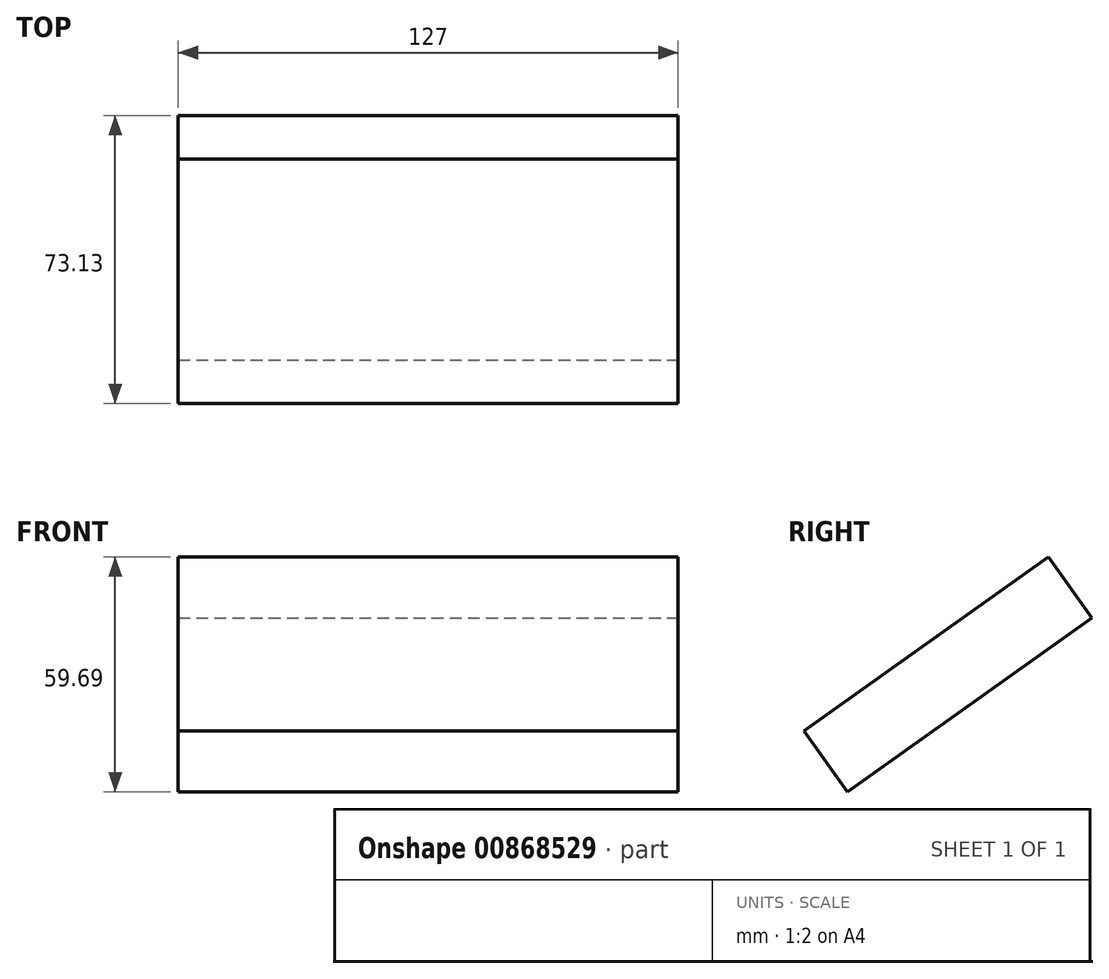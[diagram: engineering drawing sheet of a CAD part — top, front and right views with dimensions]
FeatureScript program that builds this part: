
annotation { "Feature Type Name" : "Feature", "Feature Type Description" : "" }
export const myFeature = defineFeature(function(context is Context, id is Id, definition is map)
    precondition{}
    {
        {
            var Q0;
            Q0=qCreatedBy(makeId("Right.planeOp"),FACE);
            var sketch = newSketch(context, id + "F0", { "sketchPlane" : qUnion([Q0])});
            skLineSegment(sketch, "E0", {"start": v(0, 0) * mm, "end": v(-11.04, 15.52) * mm});
            skLineSegment(sketch, "E1", {"start": v(-11.04, 15.52) * mm, "end": v(51.05, 59.7) * mm});
            skLineSegment(sketch, "E2", {"start": v(51.05, 59.7) * mm, "end": v(62.1, 44.17) * mm});
            skLineSegment(sketch, "E3", {"start": v(0, 0) * mm, "end": v(62.1, 44.17) * mm});
            skSolve(sketch);
        }
        {
            var Q0;
            Q0=makeQuery(id+"F0.imprint","IMPRINT",FACE,{"disambiguationData":[TD([[makeQuery(id+"F0.imprint","IMPRINT",EDGE,{"derivedFrom":sQuery(id+"F0.wireOp",EDGE,"E0")}),-1.0]])]});
            extrude(context, id + "F1", {"entities" : qUnion([Q0]), "oppositeDirection" : true, "depth" : 127 * mm, "offsetDistance" : 25.4 * mm});
        }
    });
